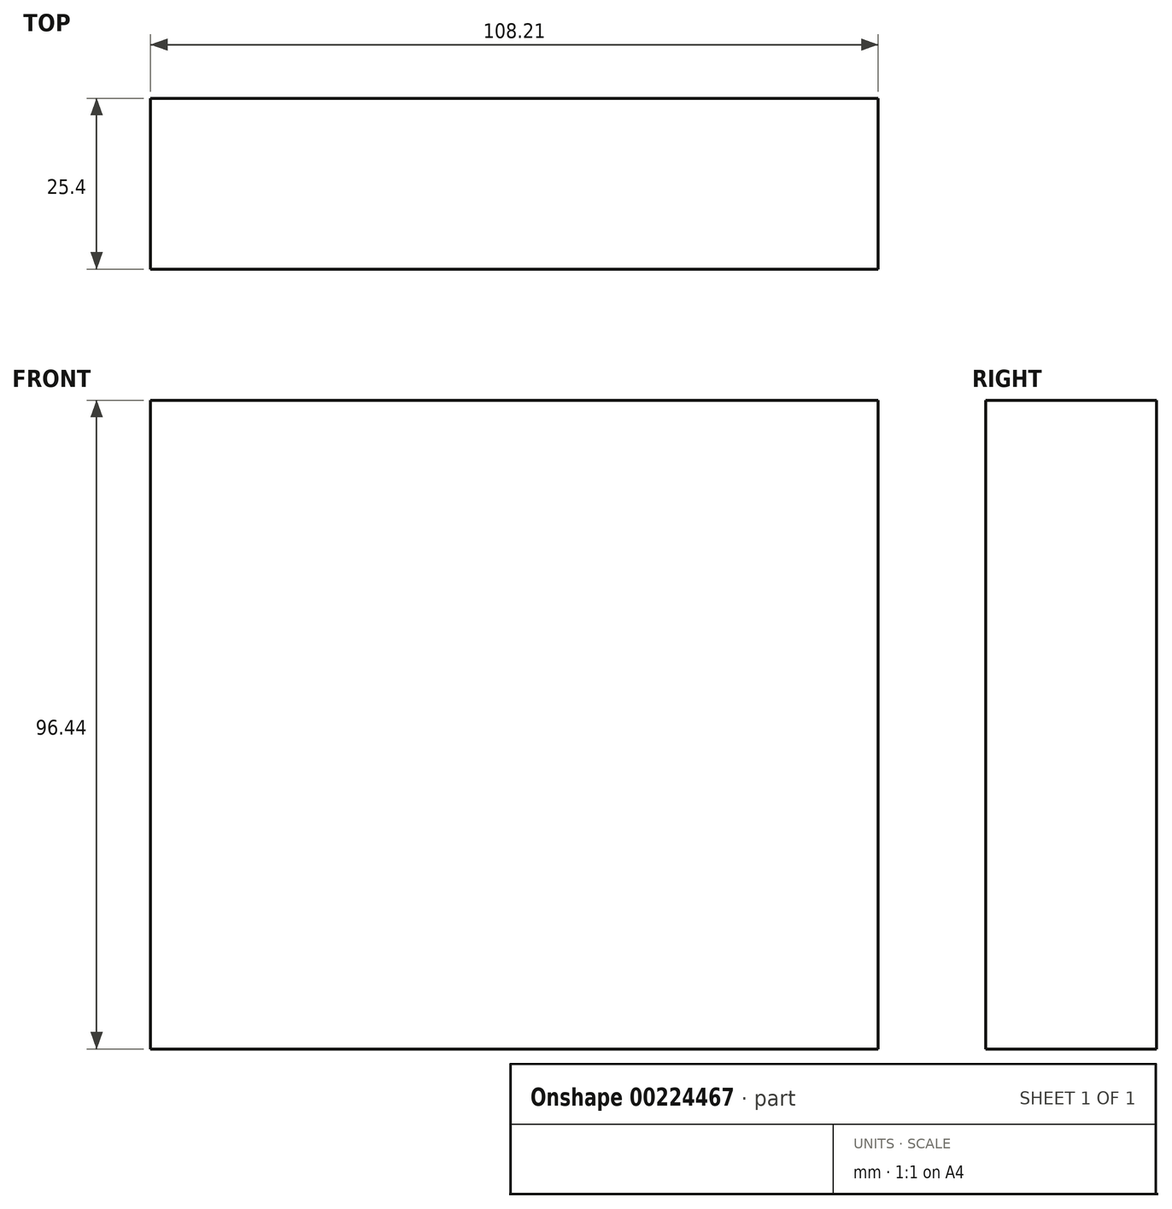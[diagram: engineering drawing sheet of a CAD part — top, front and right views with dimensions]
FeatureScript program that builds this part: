
annotation { "Feature Type Name" : "Feature", "Feature Type Description" : "" }
export const myFeature = defineFeature(function(context is Context, id is Id, definition is map)
    precondition{}
    {
        {
            var Q0;
            Q0=qCreatedBy(makeId("Front.planeOp"),FACE);
            var sketch = newSketch(context, id + "F3", { "sketchPlane" : qUnion([Q0])});
            skLineSegment(sketch, "E0.bottom", {"start": v(-11.18, 91.26) * mm, "end": v(97.03, 91.26) * mm});
            skLineSegment(sketch, "E0.top", {"start": v(-11.18, -5.18) * mm, "end": v(97.03, -5.18) * mm});
            skLineSegment(sketch, "E0.left", {"start": v(-11.18, 91.26) * mm, "end": v(-11.18, -5.18) * mm});
            skLineSegment(sketch, "E0.right", {"start": v(97.03, 91.26) * mm, "end": v(97.03, -5.18) * mm});
            skSolve(sketch);
        }
        {
            var Q0;
            Q0 = qSketchRegion(id + "F3", true);
            extrude(context, id + "F0", {"entities" : qUnion([Q0]), "depth" : 25.4 * mm});
        }
        {
            var Q0;
            Q0=qCreatedBy(makeId("Front.planeOp"),FACE);
            var sketch = newSketch(context, id + "F1", { "sketchPlane" : qUnion([Q0])});
            skFitSpline(sketch, "E1", {"points": [v(107.8, -93.83) * mm, v(-15.34, -141.65) * mm, v(-133.57, -138.96) * mm, v(-191.66, -291.56) * mm], "startDerivative": vector(-361.13, -215.19) * mm, "endDerivative": vector(-95.8, -553.05) * mm});
            skSolve(sketch);
        }
        {
            var Q0;
            Q0=sQuery(id+"F1.wireOp",EDGE,"E1");
            extrude(context, id + "F4", {"bodyType" : ToolBodyType.SURFACE, "surfaceEntities" : qUnion([Q0]), "depth" : 25.4 * mm});
        }
        {
            var Q0;
            Q0=qCreatedBy(makeId("Front.planeOp"),FACE);
            var sketch = newSketch(context, id + "F5", { "sketchPlane" : qUnion([Q0])});
            skLineSegment(sketch, "E2", {"start": v(-228.07, -83.2) * mm, "end": v(-29.66, 154.5) * mm});
            skSolve(sketch);
        }
        {
            var Q0;
            Q0 = qSketchRegion(id + "F5", true);
            var Q1;
            Q1=sQuery(id+"F5.wireOp",EDGE,"E2");
            extrude(context, id + "F2", {"entities" : qUnion([Q0]), "bodyType" : ToolBodyType.SURFACE, "surfaceEntities" : qUnion([Q1]), "depth" : 25.4 * mm});
        }
    });
